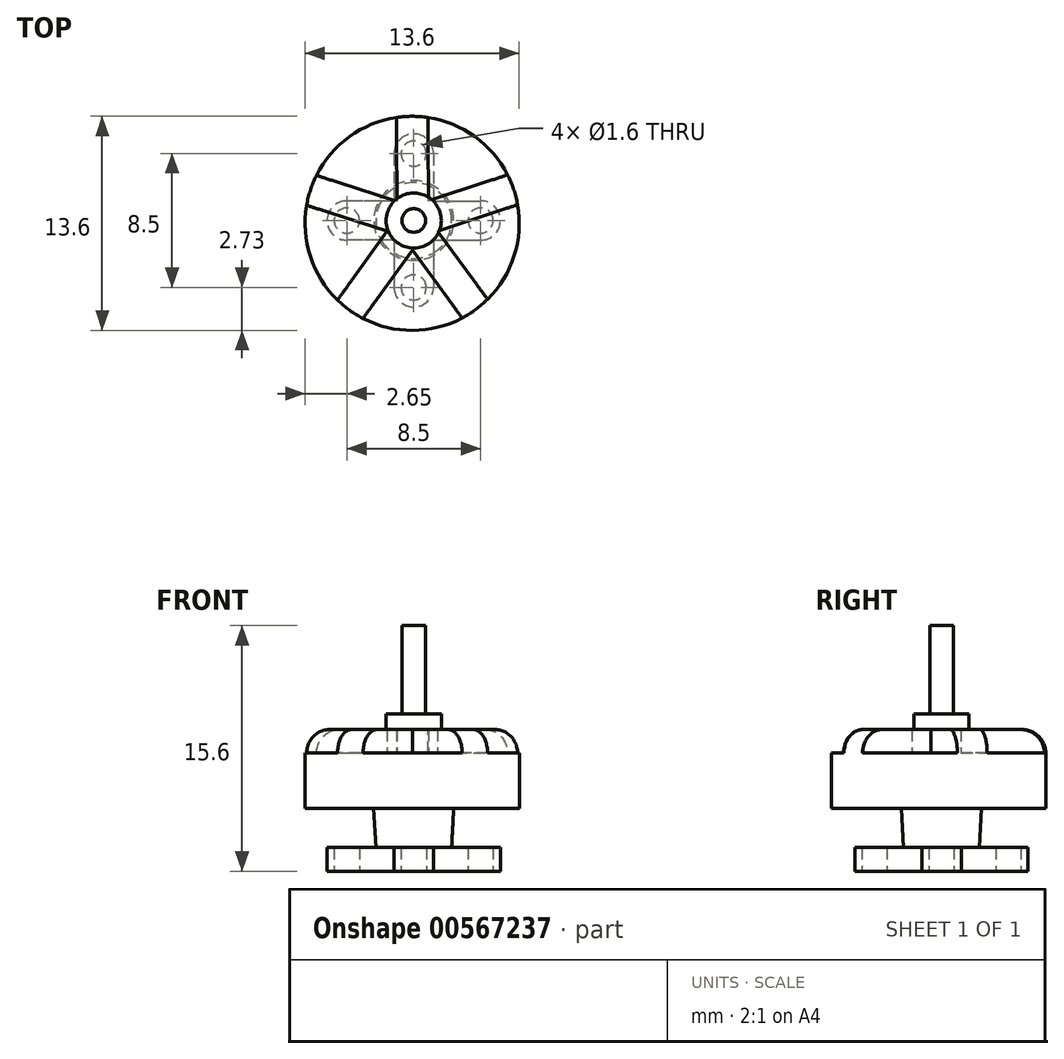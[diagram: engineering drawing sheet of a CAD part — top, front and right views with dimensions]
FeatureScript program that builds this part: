
annotation { "Feature Type Name" : "Feature", "Feature Type Description" : "" }
export const myFeature = defineFeature(function(context is Context, id is Id, definition is map)
    precondition{}
    {
        {
            var Q0;
            Q0=qCreatedBy(makeId("Top.planeOp"),FACE);
            var sketch = newSketch(context, id + "F0", { "sketchPlane" : qUnion([Q0])});
            skLineSegment(sketch, "E0.bottom", {"start": v(0, 0) * mm, "end": v(0, 0) * mm});
            skCircle(sketch, "E1", {"center": v(0, 4.25) * mm, "radius": 0.8 * mm});
            skLineSegment(sketch, "E2", {"start": v(0, 4.25) * mm, "end": v(0, 4.25) * mm});
            skCircle(sketch, "E3", {"center": v(0, -4.25) * mm, "radius": 0.8 * mm});
            skLineSegment(sketch, "E4", {"start": v(0, -4.25) * mm, "end": v(0, -4.25) * mm});
            skLineSegment(sketch, "E5.bottom", {"start": v(0, 1.25) * mm, "end": v(0, -1.25) * mm});
            skLineSegment(sketch, "E5.left", {"start": v(0, 1.25) * mm, "end": v(4.25, 1.25) * mm});
            skLineSegment(sketch, "E5.right", {"start": v(0, -1.25) * mm, "end": v(4.25, -1.25) * mm});
            skCircle(sketch, "E6", {"center": v(4.25, 0) * mm, "radius": 0.8 * mm});
            skArc(sketch, "E7", {"start": v(4.25, 1.25) * mm, "mid": v(5.5, 0) * mm, "end": v(4.25, -1.25) * mm});
            skPoint(sketch, "E8", {"position": v(0, 0) * mm});
            skLineSegment(sketch, "E9.left", {"start": v(0, -1.25) * mm, "end": v(-4.25, -1.25) * mm});
            skLineSegment(sketch, "E9.right", {"start": v(0, 1.25) * mm, "end": v(-4.25, 1.25) * mm});
            skCircle(sketch, "E10", {"center": v(-4.25, 0) * mm, "radius": 0.8 * mm});
            skArc(sketch, "E11", {"start": v(-4.25, -1.25) * mm, "mid": v(-5.5, 0) * mm, "end": v(-4.25, 1.25) * mm});
            skLineSegment(sketch, "E12", {"start": v(-1.25, 4.25) * mm, "end": v(-1.25, 1.25) * mm});
            skLineSegment(sketch, "E13", {"start": v(1.25, 4.25) * mm, "end": v(1.25, 1.25) * mm});
            skArc(sketch, "E14", {"start": v(-1.25, 4.25) * mm, "mid": v(0, 5.5) * mm, "end": v(1.25, 4.25) * mm});
            skLineSegment(sketch, "E15", {"start": v(-1.25, -1.25) * mm, "end": v(-1.25, -4.25) * mm});
            skLineSegment(sketch, "E16", {"start": v(1.25, -1.25) * mm, "end": v(1.25, -4.25) * mm});
            skArc(sketch, "E17", {"start": v(1.25, -4.25) * mm, "mid": v(0, -5.5) * mm, "end": v(-1.25, -4.25) * mm});
            skSolve(sketch);
        }
        {
            var Q0;
            {var subQ1=sQuery(id+"F0.wireOp",EDGE,"E5.bottom");Q0=makeQuery(id+"F0.imprint","IMPRINT",FACE,{"disambiguationData":[TD([[makeQuery(id+"F0.imprint","IMPRINT",EDGE,{"derivedFrom":subQ1}),-1.0]])]});}
            var Q1;
            Q1=makeQuery(id+"F0.imprint","IMPRINT",FACE,{"disambiguationData":[TD([[makeQuery(id+"F0.imprint","IMPRINT",EDGE,{"derivedFrom":sQuery(id+"F0.wireOp",EDGE,"E3")}),-1.0]])]});
            var Q2;
            {var subQ1=sQuery(id+"F0.wireOp",EDGE,"E5.bottom");Q2=makeQuery(id+"F0.imprint","IMPRINT",FACE,{"disambiguationData":[TD([[makeQuery(id+"F0.imprint","IMPRINT",EDGE,{"derivedFrom":subQ1}),1.0]])]});}
            var Q3;
            Q3=makeQuery(id+"F0.imprint","IMPRINT",FACE,{"disambiguationData":[TD([[makeQuery(id+"F0.imprint","IMPRINT",EDGE,{"derivedFrom":sQuery(id+"F0.wireOp",EDGE,"E1")}),-1.0]])]});
            extrude(context, id + "F1", {"entities" : qUnion([Q0, Q1, Q2, Q3]), "depth" : 1.5 * mm, "offsetDistance" : 25 * mm});
        }
        {
            var Q0;
            Q0=qCreatedBy(makeId("Top.planeOp"),FACE);
            var sketch = newSketch(context, id + "F2", { "sketchPlane" : qUnion([Q0])});
            skCircle(sketch, "E18", {"center": v(0, 0) * mm, "radius": 2.33 * mm});
            skSolve(sketch);
        }
        {
            var Q0;
            Q0 = qSketchRegion(id + "F2", true);
            extrude(context, id + "F3", {"entities" : qUnion([Q0]), "operationType" : NewBodyOperationType.ADD, "depth" : 4 * mm, "offsetDistance" : 25 * mm, "hasDraft" : true, "draftAngle" : 3 * degree, "hasSecondDirection" : true, "secondDirectionOppositeDirection" : true, "secondDirectionDepth" : -1.5 * mm});
        }
        {
            var Q0;
            Q0=qCreatedBy(makeId("Top.planeOp"),FACE);
            var sketch = newSketch(context, id + "F4", { "sketchPlane" : qUnion([Q0])});
            skCircle(sketch, "E19", {"center": v(-0.1, -0.18) * mm, "radius": 6.8 * mm});
            skLineSegment(sketch, "E20", {"start": v(-4.84, -5.05) * mm, "end": v(-1.07, 0.18) * mm});
            skLineSegment(sketch, "E21", {"start": v(-3.22, -6.22) * mm, "end": v(0.56, -0.98) * mm});
            skLineSegment(sketch, "E22", {"start": v(0.56, -0.98) * mm, "end": v(6.6, 1) * mm});
            skLineSegment(sketch, "E23", {"start": v(5.96, 2.9) * mm, "end": v(-0.09, 0.91) * mm});
            skLineSegment(sketch, "E24", {"start": v(-0.09, 0.91) * mm, "end": v(-6.18, 2.87) * mm});
            skLineSegment(sketch, "E25", {"start": v(-6.8, 0.96) * mm, "end": v(-0.74, -0.98) * mm});
            skLineSegment(sketch, "E26", {"start": v(-0.74, -0.98) * mm, "end": v(3.08, -6.2) * mm});
            skLineSegment(sketch, "E27", {"start": v(4.7, -5) * mm, "end": v(0.93, 0.12) * mm});
            skLineSegment(sketch, "E28", {"start": v(0.93, 0.12) * mm, "end": v(0.9, 6.54) * mm});
            skLineSegment(sketch, "E29", {"start": v(-1.1, 6.55) * mm, "end": v(-1.07, 0.18) * mm});
            skPoint(sketch, "E30", {"position": v(-1.07, 1.23) * mm});
            skPoint(sketch, "E31", {"position": v(0.93, 1.25) * mm});
            skPoint(sketch, "E32", {"position": v(1.51, -0.67) * mm});
            skPoint(sketch, "E33", {"position": v(-0.08, -1.87) * mm});
            skPoint(sketch, "E34", {"position": v(-1.69, -0.68) * mm});
            skSolve(sketch);
        }
        {
            var Q0;
            Q0=makeQuery(id+"F4.imprint","IMPRINT",FACE,{"disambiguationData":[TD([[makeQuery(id+"F4.imprint","IMPRINT",EDGE,{"derivedFrom":sQuery(id+"F4.wireOp",EDGE,"CS8Gledc-ocEL-GRrZ-OUe9-gGzYdw9osQ4W")}),1.0]])]});
            var Q1;
            {var subQ0=sQuery(id+"F4.wireOp",EDGE,"E24");var subQ1=sQuery(id+"F4.wireOp",EDGE,"E19");var subQ2=makeQuery(id+"F4.imprint","INTERSECT",VERTEX,{"derivedFrom":[subQ1,subQ0]});Q1=makeQuery(id+"F4.imprint","IMPRINT",FACE,{"disambiguationData":[TD([[makeQuery(id+"F4.imprint","IMPRINT",EDGE,{"disambiguationData":[TD([[subQ2,1.0]])],"derivedFrom":subQ1}),1.0]])]});}
            var Q2;
            {var subQ0=sQuery(id+"F4.wireOp",EDGE,"E23");var subQ1=sQuery(id+"F4.wireOp",EDGE,"E19");var subQ2=makeQuery(id+"F4.imprint","INTERSECT",VERTEX,{"derivedFrom":[subQ1,subQ0]});Q2=makeQuery(id+"F4.imprint","IMPRINT",FACE,{"disambiguationData":[TD([[makeQuery(id+"F4.imprint","IMPRINT",EDGE,{"disambiguationData":[TD([[subQ2,-1.0]])],"derivedFrom":subQ1}),1.0]])]});}
            var Q3;
            {var subQ0=sQuery(id+"F4.wireOp",EDGE,"E22");var subQ1=sQuery(id+"F4.wireOp",EDGE,"E19");var subQ2=makeQuery(id+"F4.imprint","INTERSECT",VERTEX,{"derivedFrom":[subQ1,subQ0]});Q3=makeQuery(id+"F4.imprint","IMPRINT",FACE,{"disambiguationData":[TD([[makeQuery(id+"F4.imprint","IMPRINT",EDGE,{"disambiguationData":[TD([[subQ2,1.0]])],"derivedFrom":subQ1}),1.0]])]});}
            var Q4;
            {var subQ0=sQuery(id+"F4.wireOp",EDGE,"E21");var subQ1=sQuery(id+"F4.wireOp",EDGE,"E19");var subQ2=makeQuery(id+"F4.imprint","INTERSECT",VERTEX,{"derivedFrom":[subQ1,subQ0]});Q4=makeQuery(id+"F4.imprint","IMPRINT",FACE,{"disambiguationData":[TD([[makeQuery(id+"F4.imprint","IMPRINT",EDGE,{"disambiguationData":[TD([[subQ2,-1.0]])],"derivedFrom":subQ1}),1.0]])]});}
            var Q5;
            {var subQ0=sQuery(id+"F4.wireOp",EDGE,"E20");var subQ1=sQuery(id+"F4.wireOp",EDGE,"E19");var subQ2=makeQuery(id+"F4.imprint","INTERSECT",VERTEX,{"derivedFrom":[subQ1,subQ0]});Q5=makeQuery(id+"F4.imprint","IMPRINT",FACE,{"disambiguationData":[TD([[makeQuery(id+"F4.imprint","IMPRINT",EDGE,{"disambiguationData":[TD([[subQ2,1.0]])],"derivedFrom":subQ1}),1.0]])]});}
            extrude(context, id + "F5", {"entities" : qUnion([Q0, Q1, Q2, Q3, Q4, Q5]), "operationType" : NewBodyOperationType.ADD, "depth" : 7.5 * mm, "offsetDistance" : 25 * mm, "hasSecondDirection" : true, "secondDirectionOppositeDirection" : false, "secondDirectionDepth" : 4 * mm});
        }
        {
            var Q0;
            {var subQ5=sQuery(id+"F4.wireOp",EDGE,"k3woJ1cC-TIMz-5FnJ-hXcG-qWgU7OcKqM6W");var subQ6=sQuery(id+"F4.wireOp",EDGE,"CS8Gledc-ocEL-GRrZ-OUe9-gGzYdw9osQ4W");var subQ7=makeQuery(id+"F4.imprint","INTERSECT",VERTEX,{"derivedFrom":[subQ6,subQ5]});Q0=makeQuery(id+"F4.imprint","IMPRINT",FACE,{"disambiguationData":[TD([[makeQuery(id+"F4.imprint","IMPRINT",EDGE,{"disambiguationData":[TD([[subQ7,-1.0]])],"derivedFrom":subQ6}),1.0]])]});}
            var Q1;
            {var subQ1=sQuery(id+"F4.wireOp",EDGE,"CS8Gledc-ocEL-GRrZ-OUe9-gGzYdw9osQ4W");var subQ5=sQuery(id+"F4.wireOp",EDGE,"syxK5ZXx-2APs-c3Oq-3aUw-kv2rdBUAnRqm");var subQ6=makeQuery(id+"F4.imprint","INTERSECT",VERTEX,{"derivedFrom":[subQ1,subQ5]});Q1=makeQuery(id+"F4.imprint","IMPRINT",FACE,{"disambiguationData":[TD([[makeQuery(id+"F4.imprint","IMPRINT",EDGE,{"disambiguationData":[TD([[subQ6,-1.0]])],"derivedFrom":subQ1}),1.0]])]});}
            var Q2;
            {var subQ1=sQuery(id+"F4.wireOp",EDGE,"CS8Gledc-ocEL-GRrZ-OUe9-gGzYdw9osQ4W");var subQ7=sQuery(id+"F4.wireOp",EDGE,"dCaOjtC0-uw3J-C8sN-ZGMB-qHC1DhSjRnhC");var subQ8=makeQuery(id+"F4.imprint","INTERSECT",VERTEX,{"derivedFrom":[subQ1,subQ7]});Q2=makeQuery(id+"F4.imprint","IMPRINT",FACE,{"disambiguationData":[TD([[makeQuery(id+"F4.imprint","IMPRINT",EDGE,{"disambiguationData":[TD([[subQ8,-1.0]])],"derivedFrom":subQ1}),1.0]])]});}
            var Q3;
            {var subQ13=sQuery(id+"F4.wireOp",EDGE,"raEMwXOy-ZiTj-Mc98-j2ZQ-mD7UlOAf2jAu");var subQ14=sQuery(id+"F4.wireOp",EDGE,"syxK5ZXx-2APs-c3Oq-3aUw-kv2rdBUAnRqm");var subQ15=makeQuery(id+"F4.imprint","INTERSECT",VERTEX,{"derivedFrom":[subQ14,subQ13]});Q3=makeQuery(id+"F4.imprint","IMPRINT",FACE,{"disambiguationData":[TD([[makeQuery(id+"F4.imprint","IMPRINT",EDGE,{"disambiguationData":[TD([[subQ15,1.0]])],"derivedFrom":subQ14}),-1.0]])]});}
            var Q4;
            {var subQ0=sQuery(id+"F4.wireOp",EDGE,"U70CnbfW-tcqK-zMxQ-wlnv-C4eU3dflsgoq");var subQ1=sQuery(id+"F4.wireOp",EDGE,"CS8Gledc-ocEL-GRrZ-OUe9-gGzYdw9osQ4W");var subQ2=makeQuery(id+"F4.imprint","INTERSECT",VERTEX,{"derivedFrom":[subQ1,subQ0]});Q4=makeQuery(id+"F4.imprint","IMPRINT",FACE,{"disambiguationData":[TD([[makeQuery(id+"F4.imprint","IMPRINT",EDGE,{"disambiguationData":[TD([[subQ2,1.0]])],"derivedFrom":subQ1}),1.0]])]});}
            var Q5;
            {var subQ5=sQuery(id+"F4.wireOp",EDGE,"lQARcTSB-Ecui-HiRb-6IBr-9f16AjDH4K86");var subQ6=sQuery(id+"F4.wireOp",EDGE,"CS8Gledc-ocEL-GRrZ-OUe9-gGzYdw9osQ4W");var subQ7=makeQuery(id+"F4.imprint","INTERSECT",VERTEX,{"derivedFrom":[subQ6,subQ5]});Q5=makeQuery(id+"F4.imprint","IMPRINT",FACE,{"disambiguationData":[TD([[makeQuery(id+"F4.imprint","IMPRINT",EDGE,{"disambiguationData":[TD([[subQ7,-1.0]])],"derivedFrom":subQ6}),1.0]])]});}
            var Q6;
            {var subQ5=sQuery(id+"F4.wireOp",EDGE,"E26");var subQ6=sQuery(id+"F4.wireOp",EDGE,"E19");var subQ7=makeQuery(id+"F4.imprint","INTERSECT",VERTEX,{"derivedFrom":[subQ6,subQ5]});Q6=makeQuery(id+"F4.imprint","IMPRINT",FACE,{"disambiguationData":[TD([[makeQuery(id+"F4.imprint","IMPRINT",EDGE,{"disambiguationData":[TD([[subQ7,-1.0]])],"derivedFrom":subQ6}),1.0]])]});}
            var Q7;
            {var subQ1=sQuery(id+"F4.wireOp",EDGE,"E19");var subQ7=sQuery(id+"F4.wireOp",EDGE,"E22");var subQ9=makeQuery(id+"F4.imprint","INTERSECT",VERTEX,{"derivedFrom":[subQ1,subQ7]});Q7=makeQuery(id+"F4.imprint","IMPRINT",FACE,{"disambiguationData":[TD([[makeQuery(id+"F4.imprint","IMPRINT",EDGE,{"disambiguationData":[TD([[subQ9,-1.0]])],"derivedFrom":subQ1}),1.0]])]});}
            var Q8;
            {var subQ5=sQuery(id+"F4.wireOp",EDGE,"E28");var subQ6=sQuery(id+"F4.wireOp",EDGE,"E19");var subQ7=makeQuery(id+"F4.imprint","INTERSECT",VERTEX,{"derivedFrom":[subQ6,subQ5]});Q8=makeQuery(id+"F4.imprint","IMPRINT",FACE,{"disambiguationData":[TD([[makeQuery(id+"F4.imprint","IMPRINT",EDGE,{"disambiguationData":[TD([[subQ7,-1.0]])],"derivedFrom":subQ6}),1.0]])]});}
            var Q9;
            {var subQ1=sQuery(id+"F4.wireOp",EDGE,"E19");var subQ7=sQuery(id+"F4.wireOp",EDGE,"E24");var subQ8=makeQuery(id+"F4.imprint","INTERSECT",VERTEX,{"derivedFrom":[subQ1,subQ7]});Q9=makeQuery(id+"F4.imprint","IMPRINT",FACE,{"disambiguationData":[TD([[makeQuery(id+"F4.imprint","IMPRINT",EDGE,{"disambiguationData":[TD([[subQ8,-1.0]])],"derivedFrom":subQ1}),1.0]])]});}
            var Q10;
            {var subQ1=sQuery(id+"F4.wireOp",EDGE,"E19");var subQ5=sQuery(id+"F4.wireOp",EDGE,"E20");var subQ6=makeQuery(id+"F4.imprint","INTERSECT",VERTEX,{"derivedFrom":[subQ1,subQ5]});Q10=makeQuery(id+"F4.imprint","IMPRINT",FACE,{"disambiguationData":[TD([[makeQuery(id+"F4.imprint","IMPRINT",EDGE,{"disambiguationData":[TD([[subQ6,-1.0]])],"derivedFrom":subQ1}),1.0]])]});}
            var Q11;
            {var subQ13=sQuery(id+"F4.wireOp",EDGE,"E29");var subQ14=sQuery(id+"F4.wireOp",EDGE,"E20");var subQ15=makeQuery(id+"F4.imprint","INTERSECT",VERTEX,{"derivedFrom":[subQ14,subQ13]});Q11=makeQuery(id+"F4.imprint","IMPRINT",FACE,{"disambiguationData":[TD([[makeQuery(id+"F4.imprint","IMPRINT",EDGE,{"disambiguationData":[TD([[subQ15,1.0]])],"derivedFrom":subQ14}),-1.0]])]});}
            extrude(context, id + "F6", {"entities" : qUnion([Q0, Q1, Q2, Q3, Q4, Q5, Q6, Q7, Q8, Q9, Q10, Q11]), "operationType" : NewBodyOperationType.ADD, "depth" : 9 * mm, "offsetDistance" : 25 * mm, "hasSecondDirection" : true, "secondDirectionOppositeDirection" : true, "secondDirectionDepth" : -4 * mm});
        }
        {
            var Q0;
            {var subQ0=sQuery(id+"F4.wireOp",EDGE,"CS8Gledc-ocEL-GRrZ-OUe9-gGzYdw9osQ4W");Q0=makeQuery(id+"F6.opExtrude","CAP_EDGE",EDGE,{"disambiguationData":[OSD([subQ0]),TDD([makeQuery(id+"F4.imprint","IMPRINT",EDGE,{"disambiguationData":[TD([[makeQuery(id+"F4.imprint","INTERSECT",VERTEX,{"derivedFrom":[subQ0,sQuery(id+"F4.wireOp",EDGE,"dCaOjtC0-uw3J-C8sN-ZGMB-qHC1DhSjRnhC")]}),-1.0]])],"derivedFrom":subQ0})])],"isStart":false});}
            var Q1;
            {var subQ0=sQuery(id+"F4.wireOp",EDGE,"CS8Gledc-ocEL-GRrZ-OUe9-gGzYdw9osQ4W");Q1=makeQuery(id+"F6.opExtrude","CAP_EDGE",EDGE,{"disambiguationData":[OSD([subQ0]),TDD([makeQuery(id+"F4.imprint","IMPRINT",EDGE,{"disambiguationData":[TD([[makeQuery(id+"F4.imprint","INTERSECT",VERTEX,{"derivedFrom":[subQ0,sQuery(id+"F4.wireOp",EDGE,"lQARcTSB-Ecui-HiRb-6IBr-9f16AjDH4K86")]}),-1.0]])],"derivedFrom":subQ0})])],"isStart":false});}
            var Q2;
            {var subQ0=sQuery(id+"F4.wireOp",EDGE,"CS8Gledc-ocEL-GRrZ-OUe9-gGzYdw9osQ4W");Q2=makeQuery(id+"F6.opExtrude","CAP_EDGE",EDGE,{"disambiguationData":[OSD([subQ0]),TDD([makeQuery(id+"F4.imprint","IMPRINT",EDGE,{"disambiguationData":[TD([[makeQuery(id+"F4.imprint","INTERSECT",VERTEX,{"derivedFrom":[subQ0,sQuery(id+"F4.wireOp",EDGE,"U70CnbfW-tcqK-zMxQ-wlnv-C4eU3dflsgoq")]}),1.0]])],"derivedFrom":subQ0})])],"isStart":false});}
            var Q3;
            {var subQ0=sQuery(id+"F4.wireOp",EDGE,"CS8Gledc-ocEL-GRrZ-OUe9-gGzYdw9osQ4W");Q3=makeQuery(id+"F6.opExtrude","CAP_EDGE",EDGE,{"disambiguationData":[OSD([subQ0]),TDD([makeQuery(id+"F4.imprint","IMPRINT",EDGE,{"disambiguationData":[TD([[makeQuery(id+"F4.imprint","INTERSECT",VERTEX,{"derivedFrom":[subQ0,sQuery(id+"F4.wireOp",EDGE,"k3woJ1cC-TIMz-5FnJ-hXcG-qWgU7OcKqM6W")]}),-1.0]])],"derivedFrom":subQ0})])],"isStart":false});}
            var Q4;
            {var subQ0=sQuery(id+"F4.wireOp",EDGE,"CS8Gledc-ocEL-GRrZ-OUe9-gGzYdw9osQ4W");Q4=makeQuery(id+"F6.opExtrude","CAP_EDGE",EDGE,{"disambiguationData":[OSD([subQ0]),TDD([makeQuery(id+"F4.imprint","IMPRINT",EDGE,{"disambiguationData":[TD([[makeQuery(id+"F4.imprint","INTERSECT",VERTEX,{"derivedFrom":[subQ0,sQuery(id+"F4.wireOp",EDGE,"syxK5ZXx-2APs-c3Oq-3aUw-kv2rdBUAnRqm")]}),-1.0]])],"derivedFrom":subQ0})])],"isStart":false});}
            var Q5;
            {var subQ0=sQuery(id+"F4.wireOp",EDGE,"E19");Q5=makeQuery(id+"F6.opExtrude","CAP_EDGE",EDGE,{"disambiguationData":[OSD([subQ0]),TDD([makeQuery(id+"F4.imprint","IMPRINT",EDGE,{"disambiguationData":[TD([[makeQuery(id+"F4.imprint","INTERSECT",VERTEX,{"derivedFrom":[subQ0,sQuery(id+"F4.wireOp",EDGE,"E28")]}),-1.0]])],"derivedFrom":subQ0})])],"isStart":false});}
            var Q6;
            {var subQ0=sQuery(id+"F4.wireOp",EDGE,"E19");Q6=makeQuery(id+"F6.opExtrude","CAP_EDGE",EDGE,{"disambiguationData":[OSD([subQ0]),TDD([makeQuery(id+"F4.imprint","IMPRINT",EDGE,{"disambiguationData":[TD([[makeQuery(id+"F4.imprint","INTERSECT",VERTEX,{"derivedFrom":[subQ0,sQuery(id+"F4.wireOp",EDGE,"E24")]}),-1.0]])],"derivedFrom":subQ0})])],"isStart":false});}
            var Q7;
            {var subQ0=sQuery(id+"F4.wireOp",EDGE,"E19");Q7=makeQuery(id+"F6.opExtrude","CAP_EDGE",EDGE,{"disambiguationData":[OSD([subQ0]),TDD([makeQuery(id+"F4.imprint","IMPRINT",EDGE,{"disambiguationData":[TD([[makeQuery(id+"F4.imprint","INTERSECT",VERTEX,{"derivedFrom":[subQ0,sQuery(id+"F4.wireOp",EDGE,"E20")]}),-1.0]])],"derivedFrom":subQ0})])],"isStart":false});}
            var Q8;
            {var subQ0=sQuery(id+"F4.wireOp",EDGE,"E19");Q8=makeQuery(id+"F6.opExtrude","CAP_EDGE",EDGE,{"disambiguationData":[OSD([subQ0]),TDD([makeQuery(id+"F4.imprint","IMPRINT",EDGE,{"disambiguationData":[TD([[makeQuery(id+"F4.imprint","INTERSECT",VERTEX,{"derivedFrom":[subQ0,sQuery(id+"F4.wireOp",EDGE,"E22")]}),-1.0]])],"derivedFrom":subQ0})])],"isStart":false});}
            var Q9;
            {var subQ0=sQuery(id+"F4.wireOp",EDGE,"E19");Q9=makeQuery(id+"F6.opExtrude","CAP_EDGE",EDGE,{"disambiguationData":[OSD([subQ0]),TDD([makeQuery(id+"F4.imprint","IMPRINT",EDGE,{"disambiguationData":[TD([[makeQuery(id+"F4.imprint","INTERSECT",VERTEX,{"derivedFrom":[subQ0,sQuery(id+"F4.wireOp",EDGE,"E26")]}),-1.0]])],"derivedFrom":subQ0})])],"isStart":false});}
            fillet(context, id + "F7", {"entities" : qUnion([Q0, Q1, Q2, Q3, Q4, Q5, Q6, Q7, Q8, Q9]), "radius" : 1.5 * mm, "tangentPropagation" : true, "allowEdgeOverflow" : false});
        }
        {
            var Q0;
            Q0=qCreatedBy(makeId("Top.planeOp"),FACE);
            var sketch = newSketch(context, id + "F8", { "sketchPlane" : qUnion([Q0])});
            skCircle(sketch, "E35", {"center": v(0, 0) * mm, "radius": 1.75 * mm});
            skCircle(sketch, "E36", {"center": v(0, 0) * mm, "radius": 0.75 * mm});
            skSolve(sketch);
        }
        {
            var Q0;
            Q0=makeQuery(id+"F8.imprint","IMPRINT",FACE,{"disambiguationData":[TD([[makeQuery(id+"F8.imprint","IMPRINT",EDGE,{"derivedFrom":sQuery(id+"F8.wireOp",EDGE,"E36")}),1.0]])]});
            var Q1;
            Q1=makeQuery(id+"F8.imprint","IMPRINT",FACE,{"disambiguationData":[TD([[makeQuery(id+"F8.imprint","IMPRINT",EDGE,{"derivedFrom":sQuery(id+"F8.wireOp",EDGE,"E35")}),1.0]])]});
            var Q2;
            Q2=sQuery(id+"F8.wireOp",EDGE,"E35");
            extrude(context, id + "F9", {"entities" : qUnion([Q0, Q1]), "operationType" : NewBodyOperationType.ADD, "surfaceEntities" : qUnion([Q2]), "depth" : 10 * mm, "offsetDistance" : 25 * mm, "hasSecondDirection" : true, "secondDirectionOppositeDirection" : false, "secondDirectionDepth" : 9 * mm});
        }
        {
            var Q0;
            Q0=makeQuery(id+"F8.imprint","IMPRINT",FACE,{"disambiguationData":[TD([[makeQuery(id+"F8.imprint","IMPRINT",EDGE,{"derivedFrom":sQuery(id+"F8.wireOp",EDGE,"E36")}),1.0]])]});
            extrude(context, id + "F10", {"entities" : qUnion([Q0]), "operationType" : NewBodyOperationType.ADD, "depth" : 15.6 * mm, "offsetDistance" : 25 * mm});
        }
    });
